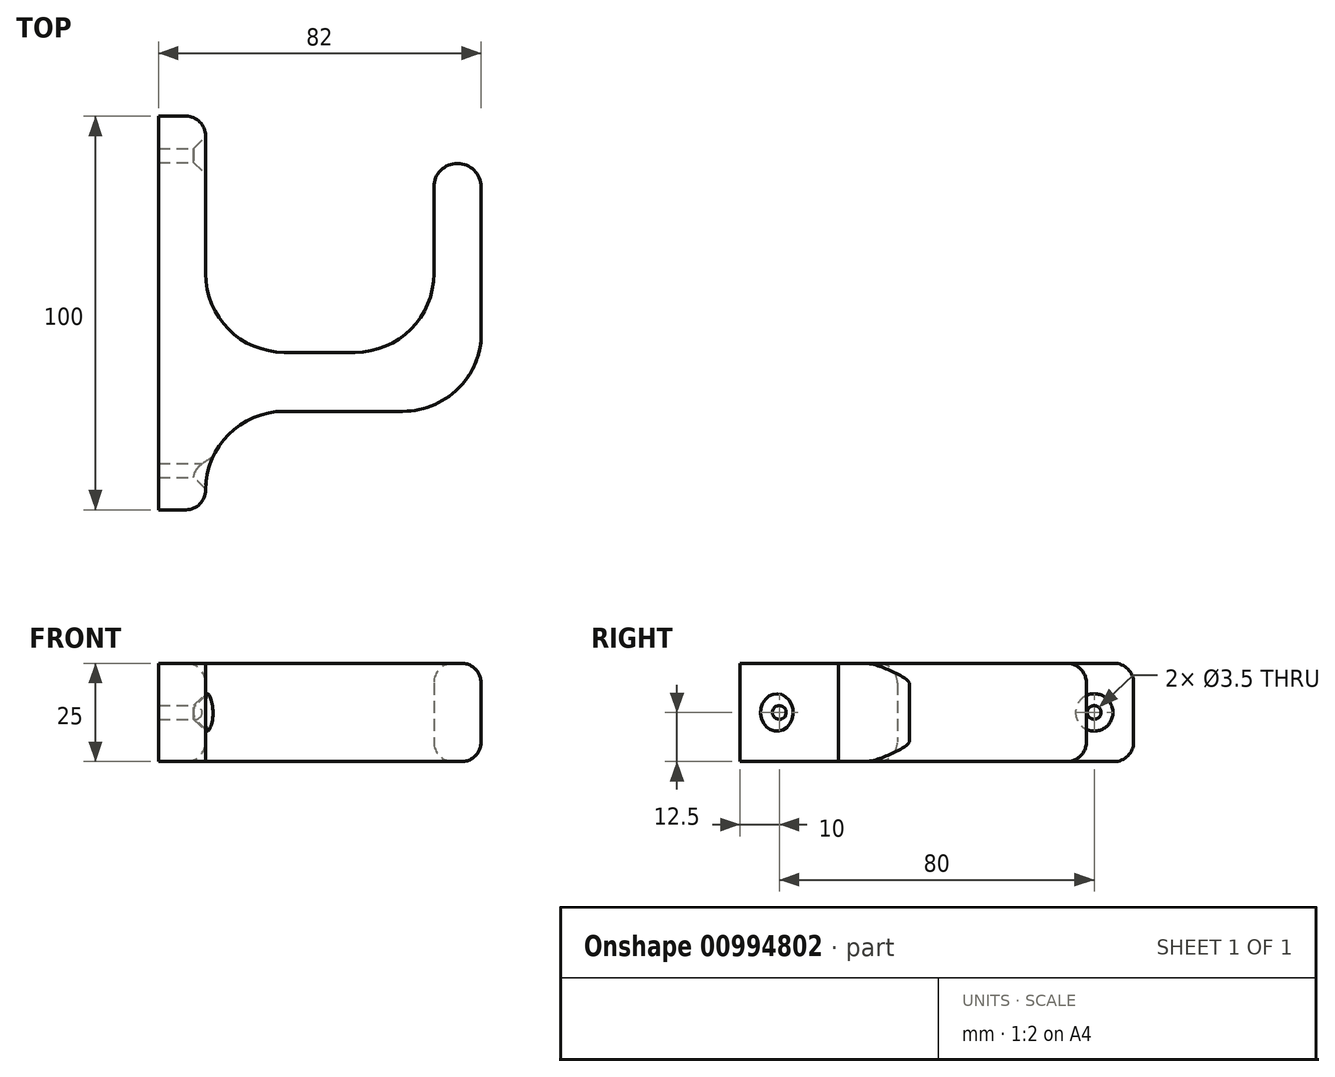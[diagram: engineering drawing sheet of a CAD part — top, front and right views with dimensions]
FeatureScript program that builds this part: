
annotation { "Feature Type Name" : "Feature", "Feature Type Description" : "" }
export const myFeature = defineFeature(function(context is Context, id is Id, definition is map)
    precondition{}
    {
        {
            var Q0;
            Q0=qCreatedBy(makeId("Top.planeOp"),FACE);
            var sketch = newSketch(context, id + "F0", { "sketchPlane" : qUnion([Q0])});
            skLineSegment(sketch, "E0.bottom", {"start": v(0, 60) * mm, "end": v(-12, 60) * mm});
            skLineSegment(sketch, "E0.top", {"start": v(0, -40) * mm, "end": v(-12, -40) * mm});
            skLineSegment(sketch, "E0.left", {"start": v(0, 60) * mm, "end": v(0, 20) * mm});
            skLineSegment(sketch, "E0.right", {"start": v(-12, 60) * mm, "end": v(-12, -40) * mm});
            skLineSegment(sketch, "E1.bottom", {"start": v(20, 0) * mm, "end": v(38, 0) * mm});
            skLineSegment(sketch, "E1.top", {"start": v(20, -15) * mm, "end": v(50.1, -15) * mm});
            skLineSegment(sketch, "E2.left", {"start": v(70, 3) * mm, "end": v(70, 42) * mm});
            skLineSegment(sketch, "E2.right", {"start": v(58, 20) * mm, "end": v(58, 42) * mm});
            skLineSegment(sketch, "E3.trimOffspring", {"start": v(0, -35) * mm, "end": v(0, -40) * mm});
            skPoint(sketch, "E4.visualSharp", {"position": v(0, 0) * mm});
            skArc(sketch, "E4.filletArc", {"start": v(0, 20) * mm, "mid": v(5.86, 5.86) * mm, "end": v(20, 0) * mm});
            skPoint(sketch, "E5.visualSharp", {"position": v(58, 0) * mm});
            skArc(sketch, "E5.filletArc", {"start": v(38, 0) * mm, "mid": v(52.14, 5.86) * mm, "end": v(58, 20) * mm});
            skPoint(sketch, "E6.visualSharp", {"position": v(70, -15) * mm});
            skArc(sketch, "E6.filletArc", {"start": v(50.1, -15) * mm, "mid": v(63.52, -9.83) * mm, "end": v(70, 3) * mm});
            skArc(sketch, "E7", {"start": v(70, 42) * mm, "mid": v(64, 48) * mm, "end": v(58, 42) * mm});
            skPoint(sketch, "E8.visualSharp", {"position": v(0, -15) * mm});
            skArc(sketch, "E8.filletArc", {"start": v(20, -15) * mm, "mid": v(5.86, -20.86) * mm, "end": v(0, -35) * mm});
            skSolve(sketch);
        }
        {
            var Q0;
            Q0 = qSketchRegion(id + "F0", true);
            extrude(context, id + "F1", {"entities" : qUnion([Q0]), "depth" : 25 * mm, "offsetDistance" : 25 * mm});
        }
        {
            var Q0;
            Q0=makeQuery(id+"F1.opExtrude","CAP_EDGE",EDGE,{"disambiguationData":[OSD([sQuery(id+"F0.wireOp",EDGE,"E1.bottom")])],"isStart":false});
            var Q1;
            Q1=makeQuery(id+"F1.opExtrude","CAP_EDGE",EDGE,{"disambiguationData":[OSD([sQuery(id+"F0.wireOp",EDGE,"E1.bottom")])],"isStart":true});
            fillet(context, id + "F2", {"entities" : qUnion([Q0, Q1]), "radius" : 5 * mm, "tangentPropagation" : true, "allowEdgeOverflow" : false});
        }
        {
            var Q0;
            Q0=makeQuery(id+"F1.opExtrude","SWEPT_FACE",FACE,{"disambiguationData":[OSD([sQuery(id+"F0.wireOp",EDGE,"E0.left")])]});
            var sketch = newSketch(context, id + "F3", { "sketchPlane" : qUnion([Q0])});
            skCircle(sketch, "E9", {"center": v(50, 12.5) * mm, "radius": 1.75 * mm});
            skPoint(sketch, "E9.centerSnap0", {"position": v(60, 12.5) * mm});
            skCircle(sketch, "E10", {"center": v(-30, 12.5) * mm, "radius": 1.75 * mm});
            skSolve(sketch);
        }
        {
            var Q0;
            Q0 = qSketchRegion(id + "F3", true);
            extrude(context, id + "F4", {"entities" : qUnion([Q0]), "operationType" : NewBodyOperationType.REMOVE, "endBound" : BoundingType.SYMMETRIC, "oppositeDirection" : true, "depth" : 25 * mm, "offsetDistance" : 25 * mm});
        }
        {
            var Q0;
            Q0=makeQuery(id+"F4.boolean.opBoolean","INTERSECT",EDGE,{"derivedFrom":[makeQuery(id+"F1.opExtrude","SWEPT_FACE",FACE,{"disambiguationData":[OSD([sQuery(id+"F0.wireOp",EDGE,"E0.left")])]}),makeQuery(id+"F4.opExtrude","SWEPT_FACE",FACE,{"disambiguationData":[OSD([sQuery(id+"F3.wireOp",EDGE,"E9")])]})]});
            var Q1;
            Q1=makeQuery(id+"F4.boolean.opBoolean","INTERSECT",EDGE,{"derivedFrom":[makeQuery(id+"F1.opExtrude","SWEPT_FACE",FACE,{"disambiguationData":[OSD([sQuery(id+"F0.wireOp",EDGE,"E8.filletArc")])]}),makeQuery(id+"F4.opExtrude","SWEPT_FACE",FACE,{"disambiguationData":[OSD([sQuery(id+"F3.wireOp",EDGE,"E10")])]})]});
            chamfer(context, id + "F5", {"entities" : qUnion([Q0, Q1]), "width" : 3 * mm, "tangentPropagation" : true});
        }
        {
            var Q0;
            Q0=makeQuery(id+"F1.opExtrude","SWEPT_EDGE",EDGE,{"disambiguationData":[OSD([sQuery(id+"F0.wireOp",EDGE,"E0.top"),sQuery(id+"F0.wireOp",EDGE,"E3.trimOffspring")])]});
            var Q1;
            Q1=makeQuery(id+"F1.opExtrude","SWEPT_EDGE",EDGE,{"disambiguationData":[OSD([sQuery(id+"F0.wireOp",EDGE,"E0.bottom"),sQuery(id+"F0.wireOp",EDGE,"E0.left")])]});
            fillet(context, id + "F6", {"entities" : qUnion([Q0, Q1]), "radius" : 5 * mm, "tangentPropagation" : true, "allowEdgeOverflow" : false});
        }
    });
